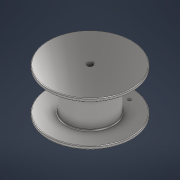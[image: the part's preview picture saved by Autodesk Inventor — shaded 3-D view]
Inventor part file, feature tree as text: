
AUTODESK INVENTOR PART (.ipt)
format: ipt  version: 2021 (Build 250183000, 183)  size: 233,984 bytes
history: native  units: mm
features: sketch x4, fillet x2, extrude x2, revolve x1, hole x1, other x1, chamfer x1
ambient origin geometry x8: Origin, YZ Plane, XZ Plane, XY Plane, X Axis, Y Axis, Z Axis, Center Point
bodies: Solid1 (feature_tree)
feature tree (12):
  revolve  "Revolution1"  [1 undecoded]
  fillet  "Fillet1"  Radius=66.0mm
  fillet  "Fillet2"  Radius=36.0mm
  extrude  "Extrusion1"  TaperAngle=90.0deg  [1 undecoded]
  hole  "Hole1"  [1 undecoded]
  other  "midPlane"
  extrude  "Extrusion2"  Depth=2.0mm
  chamfer  "Chamfer1"  Distance=3.0mm
  sketch  "Sketch1"  dims[d0=5.0mm d1=5.0mm d2=66.0mm d3=36.0mm]
  sketch  "Sketch2"  dims[d4=60.0mm d5=90.0deg]
  sketch  "Sketch3"  dims[d6=2.0mm d7=1.0mm]
  sketch  "Sketch4"  dims[d8=9.0mm d9=5.8mm d10=3.0mm d11=14.0mm d12=0.0mm d13=50.0mm d14=50.0mm d15=50.0mm d16=5.0mm d17=8.0mm d18=3.023mm d19=2.0mm d20=14.3117mm d21=8.0mm d22=0.0mm d23=22.0mm d24=7.5mm d25=0.0mm d26=0.5mm d27=2.0mm d28=45.0deg]
note: 3 required parameter values undecoded (feature->parameter linkage not recoverable at this tier; creation-order binding heuristic only, values carry confidence <= 0.55)